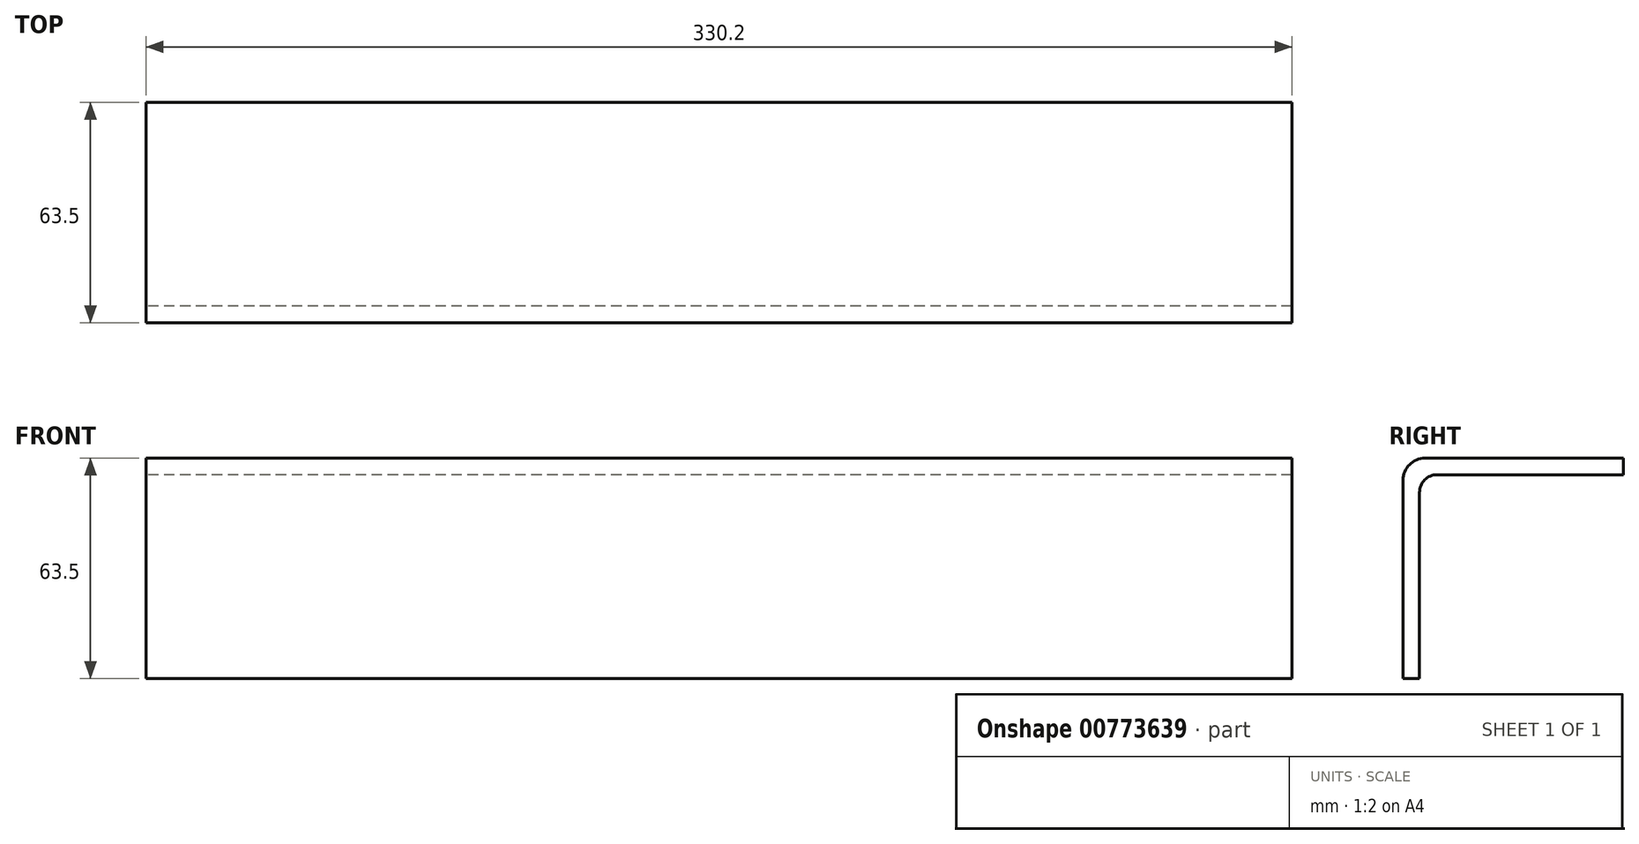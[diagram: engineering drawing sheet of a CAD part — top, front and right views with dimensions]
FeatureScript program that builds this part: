
annotation { "Feature Type Name" : "Feature", "Feature Type Description" : "" }
export const myFeature = defineFeature(function(context is Context, id is Id, definition is map)
    precondition{}
    {
        {
            var Q0;
            Q0=qCreatedBy(makeId("Right.planeOp"),FACE);
            var sketch = newSketch(context, id + "F0", { "sketchPlane" : qUnion([Q0])});
            skLineSegment(sketch, "E0", {"start": v(-28.12, -12.25) * mm, "end": v(-28.12, 44.9) * mm});
            skLineSegment(sketch, "E1", {"start": v(-21.77, 51.25) * mm, "end": v(35.38, 51.25) * mm});
            skPoint(sketch, "E2.visualSharp", {"position": v(-28.12, 51.25) * mm});
            skArc(sketch, "E2.filletArc", {"start": v(-21.77, 51.25) * mm, "mid": v(-26.26, 49.39) * mm, "end": v(-28.12, 44.9) * mm});
            skLineSegment(sketch, "E3", {"start": v(-28.12, -12.25) * mm, "end": v(-23.35, -12.25) * mm});
            skLineSegment(sketch, "E4", {"start": v(35.38, 51.25) * mm, "end": v(35.38, 46.48) * mm});
            skLineSegment(sketch, "E5", {"start": v(-23.35, -12.25) * mm, "end": v(-23.35, 41.4) * mm});
            skLineSegment(sketch, "E6", {"start": v(35.38, 46.48) * mm, "end": v(-18.27, 46.48) * mm});
            skPoint(sketch, "E7.newPointA", {"position": v(-23.35, 46.42) * mm});
            skPoint(sketch, "E7.newPointB", {"position": v(-23.29, 46.48) * mm});
            skArc(sketch, "E7.filletArc", {"start": v(-18.27, 46.48) * mm, "mid": v(-21.87, 45) * mm, "end": v(-23.35, 41.4) * mm});
            skSolve(sketch);
        }
        {
            var Q0;
            Q0=qSketchRegion(id+"F0",true);
            extrude(context, id + "F1", {"entities" : qUnion([Q0]), "depth" : 330.2 * mm, "offsetDistance" : 25.4 * mm});
        }
    });
